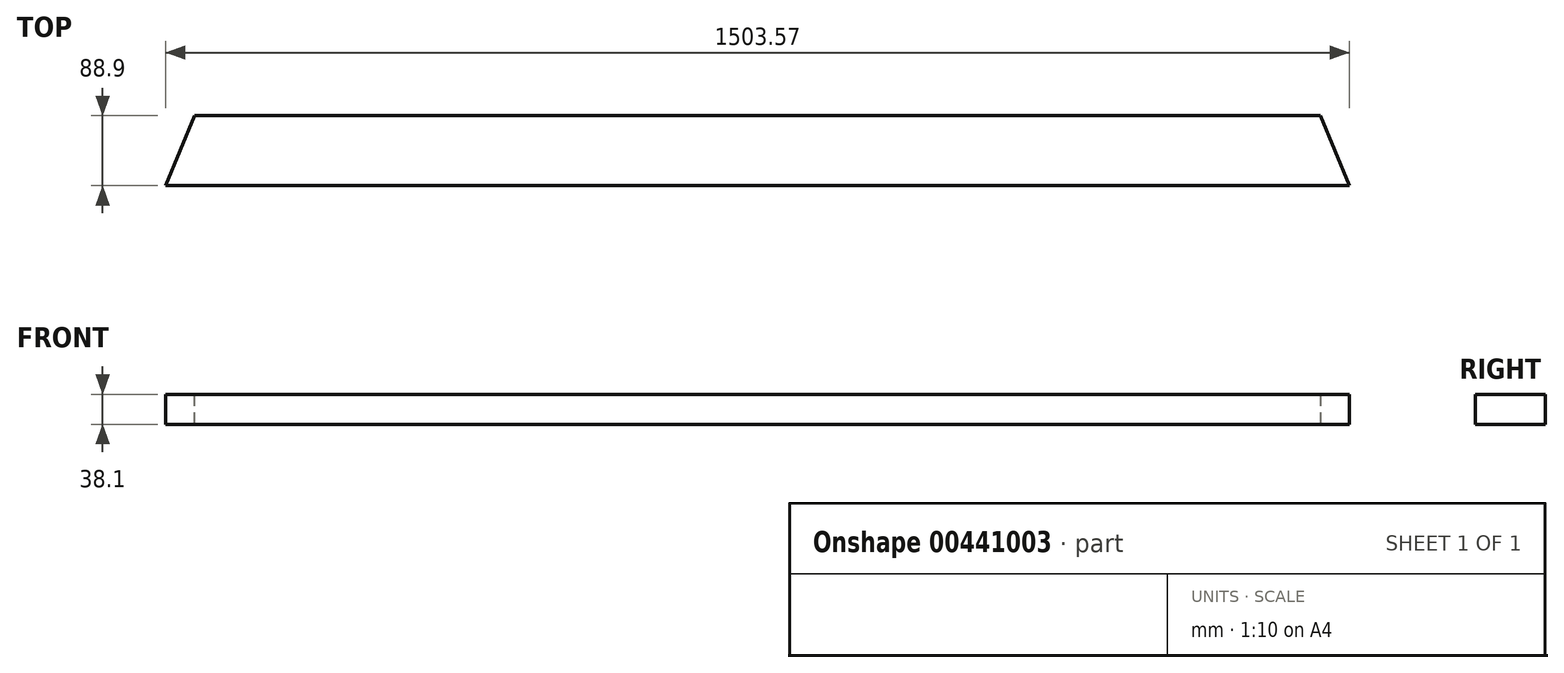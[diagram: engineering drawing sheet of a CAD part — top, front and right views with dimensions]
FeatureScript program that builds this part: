
annotation { "Feature Type Name" : "Feature", "Feature Type Description" : "" }
export const myFeature = defineFeature(function(context is Context, id is Id, definition is map)
    precondition{}
    {
        {
            var Q0;
            Q0=qCreatedBy(makeId("Top.planeOp"),FACE);
            var sketch = newSketch(context, id + "F0", { "sketchPlane" : qUnion([Q0])});
            skLineSegment(sketch, "E0.bottom", {"start": v(0, 0) * mm, "end": v(1503.57, 0) * mm});
            skLineSegment(sketch, "E0.top", {"start": v(0, 88.9) * mm, "end": v(1503.57, 88.9) * mm});
            skLineSegment(sketch, "E0.left", {"start": v(0, 0) * mm, "end": v(0, 88.9) * mm});
            skLineSegment(sketch, "E0.right", {"start": v(1503.57, 0) * mm, "end": v(1503.57, 88.9) * mm});
            skSolve(sketch);
        }
        {
            var Q0;
            Q0=makeQuery(id+"F0.imprint","IMPRINT",FACE,{"disambiguationData":[TD([[makeQuery(id+"F0.imprint","IMPRINT",EDGE,{"derivedFrom":sQuery(id+"F0.wireOp",EDGE,"E0.bottom")}),1.0]])]});
            extrude(context, id + "F1", {"entities" : qUnion([Q0]), "depth" : 38.1 * mm});
        }
        {
            var Q0;
            Q0=makeQuery(id+"F1.opExtrude","SWEPT_EDGE",EDGE,{"disambiguationData":[OSD([sQuery(id+"F0.wireOp",EDGE,"E0.top"),sQuery(id+"F0.wireOp",EDGE,"E0.right")])]});
            var Q1;
            Q1=makeQuery(id+"F1.opExtrude","SWEPT_EDGE",EDGE,{"disambiguationData":[OSD([sQuery(id+"F0.wireOp",EDGE,"E0.top"),sQuery(id+"F0.wireOp",EDGE,"E0.left")])]});
            chamfer(context, id + "F2", {"entities" : qUnion([Q0, Q1]), "chamferType" : ChamferType.OFFSET_ANGLE, "width" : 88.9 * mm, "oppositeDirection" : true, "angle" : 22.5 * degree, "tangentPropagation" : true});
        }
    });
